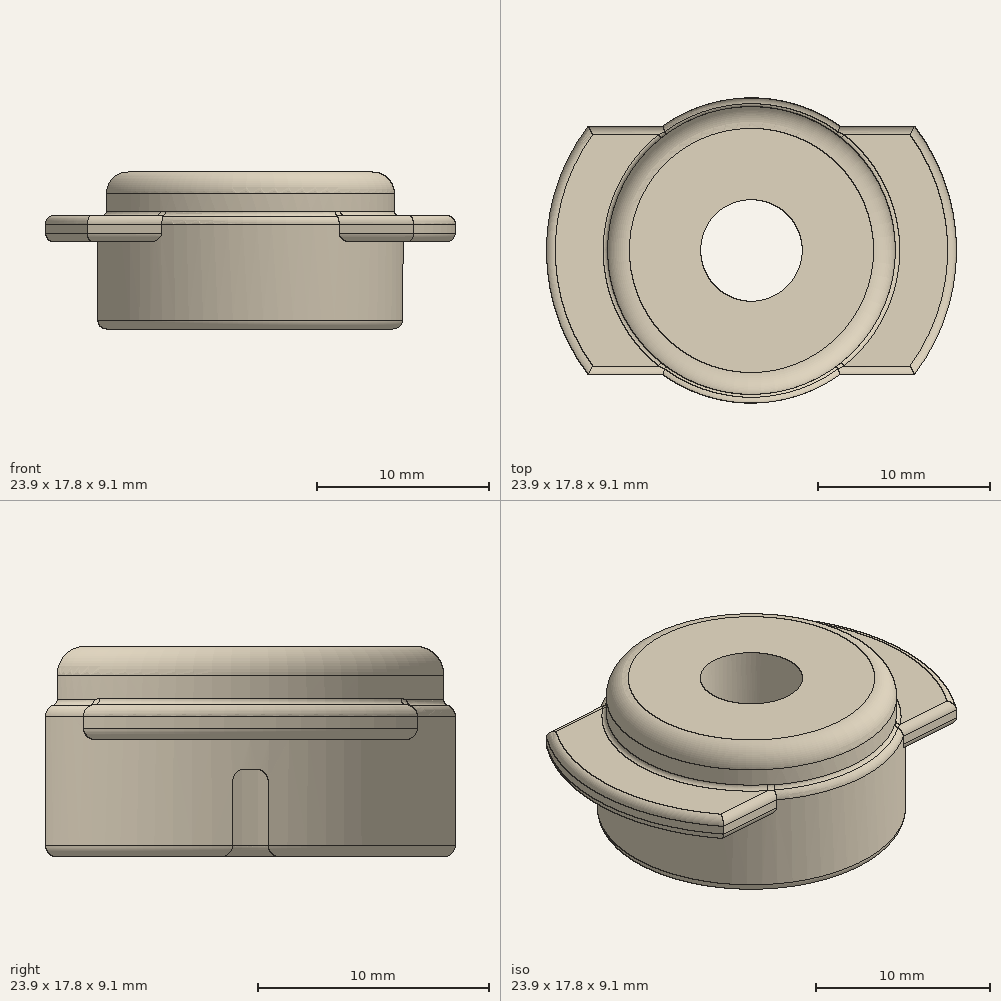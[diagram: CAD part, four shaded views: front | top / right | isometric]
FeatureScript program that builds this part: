
annotation { "Feature Type Name" : "Feature", "Feature Type Description" : "" }
export const myFeature = defineFeature(function(context is Context, id is Id, definition is map)
    precondition{}
    {
        {
            var Q0;
            Q0=qCreatedBy(makeId("Top.planeOp"),FACE);
            var sketch = newSketch(context, id + "F0", { "sketchPlane" : qUnion([Q0])});
            skCircle(sketch, "E0", {"center": v(0, 0) * mm, "radius": 11.94 * mm});
            skSolve(sketch);
        }
        {
            var Q0;
            Q0=makeQuery(id+"F0.imprint","IMPRINT",FACE,{"disambiguationData":[TD([[makeQuery(id+"F0.imprint","IMPRINT",EDGE,{"derivedFrom":sQuery(id+"F0.wireOp",EDGE,"E0")}),1.0]])]});
            var sketch = newSketch(context, id + "F1", { "sketchPlane" : qUnion([Q0])});
            skLineSegment(sketch, "E1", {"start": v(9.5, 7.24) * mm, "end": v(-9.5, 7.24) * mm});
            skLineSegment(sketch, "E2", {"start": v(9.5, -7.24) * mm, "end": v(-9.5, -7.24) * mm});
            skLineSegment(sketch, "E3", {"start": v(-9.5, 7.24) * mm, "end": v(-9.5, -7.24) * mm, "construction": true});
            skLineSegment(sketch, "E4", {"start": v(9.5, 7.24) * mm, "end": v(9.5, -7.24) * mm, "construction": true});
            skSolve(sketch);
        }
        {
            var Q0;
            Q0=qSketchRegion(id+"F0",true);
            extrude(context, id + "F2", {"entities" : qUnion([Q0]), "depth" : 1.52 * mm, "offsetDistance" : 25.4 * mm});
        }
        {
            var Q0;
            {var subQ0=sQuery(id+"F1.wireOp",EDGE,"E1");Q0=makeQuery(id+"F1.imprint","IMPRINT",FACE,{"disambiguationData":[TD([[makeQuery(id+"F1.imprint","IMPRINT",EDGE,{"derivedFrom":subQ0}),-1.0]])]});}
            var Q1;
            {var subQ0=sQuery(id+"F1.wireOp",EDGE,"E2");Q1=makeQuery(id+"F1.imprint","IMPRINT",FACE,{"disambiguationData":[TD([[makeQuery(id+"F1.imprint","IMPRINT",EDGE,{"derivedFrom":subQ0}),1.0]])]});}
            extrude(context, id + "F3", {"entities" : qUnion([Q0, Q1]), "operationType" : NewBodyOperationType.REMOVE, "depth" : 2.54 * mm, "offsetDistance" : 25.4 * mm, "hasSecondDirection" : true, "secondDirectionOppositeDirection" : true, "secondDirectionDepth" : 25.4 * mm});
        }
        {
            var Q0;
            Q0=makeQuery(id+"F2.opExtrude","CAP_FACE",FACE,{"disambiguationData":[OSD([sQuery(id+"F0.wireOp",EDGE,"E0")])],"isStart":true});
            var sketch = newSketch(context, id + "F4", { "sketchPlane" : qUnion([Q0])});
            skCircle(sketch, "E5", {"center": v(0, 0) * mm, "radius": 8.9 * mm});
            skSolve(sketch);
        }
        {
            var Q0;
            Q0=qSketchRegion(id+"F4",true);
            extrude(context, id + "F5", {"entities" : qUnion([Q0]), "operationType" : NewBodyOperationType.ADD, "oppositeDirection" : true, "depth" : 1.52 * mm, "offsetDistance" : 25.4 * mm});
        }
        {
            var Q0;
            Q0=makeQuery(id+"F5.boolean.opBoolean","MERGE",FACE,{"derivedFrom":[makeQuery(id+"F2.opExtrude","CAP_FACE",FACE,{"disambiguationData":[OSD([sQuery(id+"F0.wireOp",EDGE,"E0")])],"isStart":true}),makeQuery(id+"F5.opExtrude","CAP_FACE",FACE,{"disambiguationData":[OSD([sQuery(id+"F4.wireOp",EDGE,"E5")])],"isStart":true})]});
            var sketch = newSketch(context, id + "F6", { "sketchPlane" : qUnion([Q0])});
            skCircle(sketch, "E6", {"center": v(0, 0) * mm, "radius": 8.9 * mm});
            skSolve(sketch);
        }
        {
            var Q0;
            Q0=qSketchRegion(id+"F6",true);
            extrude(context, id + "F7", {"entities" : qUnion([Q0]), "operationType" : NewBodyOperationType.ADD, "depth" : 5.08 * mm, "offsetDistance" : 25.4 * mm});
        }
        {
            var Q0;
            Q0=makeQuery(id+"F7.opExtrude","CAP_FACE",FACE,{"disambiguationData":[OSD([sQuery(id+"F6.wireOp",EDGE,"E6")])],"isStart":false});
            var sketch = newSketch(context, id + "F8", { "sketchPlane" : qUnion([Q0])});
            skCircle(sketch, "E7", {"center": v(0, 0) * mm, "radius": 7.37 * mm});
            skSolve(sketch);
        }
        {
            var Q0;
            Q0=qSketchRegion(id+"F8",true);
            extrude(context, id + "F9", {"entities" : qUnion([Q0]), "operationType" : NewBodyOperationType.REMOVE, "oppositeDirection" : true, "depth" : 5.08 * mm, "offsetDistance" : 25.4 * mm});
        }
        {
            var Q0;
            Q0=makeQuery(id+"F7.opExtrude","CAP_FACE",FACE,{"disambiguationData":[OSD([sQuery(id+"F6.wireOp",EDGE,"E6")])],"isStart":false});
            var sketch = newSketch(context, id + "F10", { "sketchPlane" : qUnion([Q0])});
            skLineSegment(sketch, "E8", {"start": v(8.86, -0.76) * mm, "end": v(7.33, -0.76) * mm});
            skLineSegment(sketch, "E9", {"start": v(8.86, 0.76) * mm, "end": v(7.33, 0.76) * mm});
            skLineSegment(sketch, "E10", {"start": v(0, 0) * mm, "end": v(8.9, 0) * mm, "construction": true});
            skArc(sketch, "E11", {"start": v(8.86, -0.76) * mm, "mid": v(8.9, 0) * mm, "end": v(8.86, 0.76) * mm});
            skArc(sketch, "E12", {"start": v(7.33, -0.76) * mm, "mid": v(7.37, 0) * mm, "end": v(7.33, 0.76) * mm});
            skSolve(sketch);
        }
        {
            var Q0;
            Q0=qCreatedBy(makeId("Front.planeOp"),FACE);
            var sketch = newSketch(context, id + "F11", { "sketchPlane" : qUnion([Q0])});
            skLineSegment(sketch, "E13", {"start": v(0, 0) * mm, "end": v(0, -7.62) * mm, "construction": true});
            skSolve(sketch);
        }
        {
            var Q0;
            Q0=makeQuery(id+"F10.imprint","IMPRINT",FACE,{"disambiguationData":[TD([[makeQuery(id+"F10.imprint","IMPRINT",EDGE,{"derivedFrom":sQuery(id+"F10.wireOp",EDGE,"E8")}),-1.0]])]});
            var Q1;
            Q1=makeQuery(id+"FOOJxRczT3KKHVt_1.3.F10.imprint","IMPRINT",FACE,{"disambiguationData":[TD([[makeQuery(id+"FOOJxRczT3KKHVt_1.3.F10.imprint","IMPRINT",EDGE,{"derivedFrom":sQuery(id+"FOOJxRczT3KKHVt_1.3.F10.wireOp",EDGE,"E8")}),-1.0]])]});
            var Q2;
            Q2=makeQuery(id+"FOOJxRczT3KKHVt_1.2.F10.imprint","IMPRINT",FACE,{"disambiguationData":[TD([[makeQuery(id+"FOOJxRczT3KKHVt_1.2.F10.imprint","IMPRINT",EDGE,{"derivedFrom":sQuery(id+"FOOJxRczT3KKHVt_1.2.F10.wireOp",EDGE,"E8")}),-1.0]])]});
            var Q3;
            Q3=makeQuery(id+"FOOJxRczT3KKHVt_1.1.F10.imprint","IMPRINT",FACE,{"disambiguationData":[TD([[makeQuery(id+"FOOJxRczT3KKHVt_1.1.F10.imprint","IMPRINT",EDGE,{"derivedFrom":sQuery(id+"FOOJxRczT3KKHVt_1.1.F10.wireOp",EDGE,"E8")}),-1.0]])]});
            extrude(context, id + "F12", {"entities" : qUnion([Q0, Q1, Q2, Q3]), "operationType" : NewBodyOperationType.REMOVE, "oppositeDirection" : true, "depth" : 3.8 * mm, "offsetDistance" : 25.4 * mm});
        }
        {
            var Q0;
            Q0=makeQuery(id+"F12.boolean.opBoolean","COPY",EDGE,{"derivedFrom":makeQuery(id+"F12.opExtrude","CAP_EDGE",EDGE,{"disambiguationData":[OSD([sQuery(id+"FOOJxRczT3KKHVt_1.2.F10.wireOp",EDGE,"E9")])],"isStart":false})});
            var Q1;
            Q1=makeQuery(id+"F12.boolean.opBoolean","COPY",EDGE,{"derivedFrom":makeQuery(id+"F12.opExtrude","CAP_EDGE",EDGE,{"disambiguationData":[OSD([sQuery(id+"FOOJxRczT3KKHVt_1.2.F10.wireOp",EDGE,"E8")])],"isStart":false})});
            var Q2;
            Q2=makeQuery(id+"F12.boolean.opBoolean","COPY",EDGE,{"derivedFrom":makeQuery(id+"F12.opExtrude","CAP_EDGE",EDGE,{"disambiguationData":[OSD([sQuery(id+"FOOJxRczT3KKHVt_1.1.F10.wireOp",EDGE,"E9")])],"isStart":false})});
            var Q3;
            Q3=makeQuery(id+"F12.boolean.opBoolean","COPY",EDGE,{"derivedFrom":makeQuery(id+"F12.opExtrude","CAP_EDGE",EDGE,{"disambiguationData":[OSD([sQuery(id+"FOOJxRczT3KKHVt_1.3.F10.wireOp",EDGE,"E8")])],"isStart":false})});
            var Q4;
            Q4=makeQuery(id+"F12.boolean.opBoolean","COPY",EDGE,{"derivedFrom":makeQuery(id+"F12.opExtrude","CAP_EDGE",EDGE,{"disambiguationData":[OSD([sQuery(id+"F10.wireOp",EDGE,"E9")])],"isStart":false})});
            var Q5;
            Q5=makeQuery(id+"F12.boolean.opBoolean","COPY",EDGE,{"derivedFrom":makeQuery(id+"F12.opExtrude","CAP_EDGE",EDGE,{"disambiguationData":[OSD([sQuery(id+"FOOJxRczT3KKHVt_1.3.F10.wireOp",EDGE,"E9")])],"isStart":false})});
            var Q6;
            Q6=makeQuery(id+"F12.boolean.opBoolean","COPY",EDGE,{"derivedFrom":makeQuery(id+"F12.opExtrude","CAP_EDGE",EDGE,{"disambiguationData":[OSD([sQuery(id+"F10.wireOp",EDGE,"E8")])],"isStart":false})});
            var Q7;
            Q7=makeQuery(id+"F12.boolean.opBoolean","COPY",EDGE,{"derivedFrom":makeQuery(id+"F12.opExtrude","CAP_EDGE",EDGE,{"disambiguationData":[OSD([sQuery(id+"FOOJxRczT3KKHVt_1.1.F10.wireOp",EDGE,"E8")])],"isStart":false})});
            fillet(context, id + "F13", {"entities" : qUnion([Q0, Q1, Q2, Q3, Q4, Q5, Q6, Q7]), "radius" : 0.5 * mm, "tangentPropagation" : true, "allowEdgeOverflow" : false});
        }
        {
            var Q0;
            Q0=makeQuery(id+"F12.boolean.opBoolean","COPY",EDGE,{"derivedFrom":makeQuery(id+"F12.opExtrude","SWEPT_EDGE",EDGE,{"disambiguationData":[OSD([sQuery(id+"F6.wireOp",EDGE,"E6"),sQuery(id+"F10.wireOp",EDGE,"E8"),sQuery(id+"F10.wireOp",EDGE,"E11")])]})});
            var Q1;
            Q1=makeQuery(id+"F12.boolean.opBoolean","COPY",EDGE,{"derivedFrom":makeQuery(id+"F12.opExtrude","SWEPT_EDGE",EDGE,{"disambiguationData":[OSD([sQuery(id+"F6.wireOp",EDGE,"E6"),sQuery(id+"F10.wireOp",EDGE,"E9"),sQuery(id+"F10.wireOp",EDGE,"E11")])]})});
            var Q2;
            Q2=makeQuery(id+"F12.boolean.opBoolean","COPY",EDGE,{"derivedFrom":makeQuery(id+"F12.opExtrude","SWEPT_EDGE",EDGE,{"disambiguationData":[OSD([sQuery(id+"F8.wireOp",EDGE,"E7"),sQuery(id+"F10.wireOp",EDGE,"E8"),sQuery(id+"F10.wireOp",EDGE,"E12")])]})});
            var Q3;
            Q3=makeQuery(id+"F12.boolean.opBoolean","COPY",EDGE,{"derivedFrom":makeQuery(id+"F12.opExtrude","SWEPT_EDGE",EDGE,{"disambiguationData":[OSD([sQuery(id+"F8.wireOp",EDGE,"E7"),sQuery(id+"F10.wireOp",EDGE,"E9"),sQuery(id+"F10.wireOp",EDGE,"E12")])]})});
            var Q4;
            {var subQ0=sQuery(id+"F6.wireOp",EDGE,"E6");Q4=makeQuery(id+"F12.boolean.opBoolean","SPLIT",EDGE,{"disambiguationData":[TD([makeQuery(id+"F12.opExtrude","SWEPT_FACE",FACE,{"disambiguationData":[OSD([sQuery(id+"F10.wireOp",EDGE,"E8")])]})])],"derivedFrom":makeQuery(id+"F7.opExtrude","CAP_EDGE",EDGE,{"disambiguationData":[OSD([subQ0])],"isStart":false})});}
            var Q5;
            {var subQ0=sQuery(id+"F8.wireOp",EDGE,"E7");Q5=makeQuery(id+"F12.boolean.opBoolean","SPLIT",EDGE,{"disambiguationData":[TD([makeQuery(id+"F12.opExtrude","SWEPT_FACE",FACE,{"disambiguationData":[OSD([sQuery(id+"F10.wireOp",EDGE,"E8")])]})])],"derivedFrom":makeQuery(id+"F9.boolean.opBoolean","COPY",EDGE,{"derivedFrom":makeQuery(id+"F9.opExtrude","CAP_EDGE",EDGE,{"disambiguationData":[OSD([subQ0])],"isStart":true})})});}
            var Q6;
            {var subQ0=sQuery(id+"F6.wireOp",EDGE,"E6");Q6=makeQuery(id+"F12.boolean.opBoolean","SPLIT",EDGE,{"disambiguationData":[TD([makeQuery(id+"F12.opExtrude","SWEPT_FACE",FACE,{"disambiguationData":[OSD([sQuery(id+"F10.wireOp",EDGE,"E9")])]})])],"derivedFrom":makeQuery(id+"F7.opExtrude","CAP_EDGE",EDGE,{"disambiguationData":[OSD([subQ0])],"isStart":false})});}
            var Q7;
            {var subQ0=sQuery(id+"F8.wireOp",EDGE,"E7");Q7=makeQuery(id+"F12.boolean.opBoolean","SPLIT",EDGE,{"disambiguationData":[TD([makeQuery(id+"F12.opExtrude","SWEPT_FACE",FACE,{"disambiguationData":[OSD([sQuery(id+"F10.wireOp",EDGE,"E9")])]})])],"derivedFrom":makeQuery(id+"F9.boolean.opBoolean","COPY",EDGE,{"derivedFrom":makeQuery(id+"F9.opExtrude","CAP_EDGE",EDGE,{"disambiguationData":[OSD([subQ0])],"isStart":true})})});}
            var Q8;
            Q8=makeQuery(id+"F12.boolean.opBoolean","COPY",EDGE,{"derivedFrom":makeQuery(id+"F12.opExtrude","CAP_EDGE",EDGE,{"disambiguationData":[OSD([sQuery(id+"F10.wireOp",EDGE,"E9")])],"isStart":true})});
            var Q9;
            Q9=makeQuery(id+"F12.boolean.opBoolean","COPY",EDGE,{"derivedFrom":makeQuery(id+"F12.opExtrude","CAP_EDGE",EDGE,{"disambiguationData":[OSD([sQuery(id+"F10.wireOp",EDGE,"E8")])],"isStart":true})});
            var Q10;
            {var subQ0=sQuery(id+"F6.wireOp",EDGE,"E6");Q10=makeQuery(id+"F12.boolean.opBoolean","SPLIT",EDGE,{"disambiguationData":[TD([makeQuery(id+"F12.opExtrude","SWEPT_FACE",FACE,{"disambiguationData":[OSD([sQuery(id+"FOOJxRczT3KKHVt_1.2.F10.wireOp",EDGE,"E9")])]})])],"derivedFrom":makeQuery(id+"F7.opExtrude","CAP_EDGE",EDGE,{"disambiguationData":[OSD([subQ0])],"isStart":false})});}
            var Q11;
            {var subQ0=sQuery(id+"F8.wireOp",EDGE,"E7");Q11=makeQuery(id+"F12.boolean.opBoolean","SPLIT",EDGE,{"disambiguationData":[TD([makeQuery(id+"F12.opExtrude","SWEPT_FACE",FACE,{"disambiguationData":[OSD([sQuery(id+"FOOJxRczT3KKHVt_1.2.F10.wireOp",EDGE,"E9")])]})])],"derivedFrom":makeQuery(id+"F9.boolean.opBoolean","COPY",EDGE,{"derivedFrom":makeQuery(id+"F9.opExtrude","CAP_EDGE",EDGE,{"disambiguationData":[OSD([subQ0])],"isStart":true})})});}
            var Q12;
            Q12=makeQuery(id+"F12.boolean.opBoolean","COPY",EDGE,{"derivedFrom":makeQuery(id+"F12.opExtrude","CAP_EDGE",EDGE,{"disambiguationData":[OSD([sQuery(id+"FOOJxRczT3KKHVt_1.3.F10.wireOp",EDGE,"E8")])],"isStart":true})});
            var Q13;
            Q13=makeQuery(id+"F12.boolean.opBoolean","COPY",EDGE,{"derivedFrom":makeQuery(id+"F12.opExtrude","CAP_EDGE",EDGE,{"disambiguationData":[OSD([sQuery(id+"FOOJxRczT3KKHVt_1.3.F10.wireOp",EDGE,"E9")])],"isStart":true})});
            var Q14;
            Q14=makeQuery(id+"F12.boolean.opBoolean","COPY",EDGE,{"derivedFrom":makeQuery(id+"F12.opExtrude","SWEPT_EDGE",EDGE,{"disambiguationData":[OSD([sQuery(id+"FOOJxRczT3KKHVt_1.3.F10.wireOp",EDGE,"E8"),sQuery(id+"FOOJxRczT3KKHVt_1.3.F10.wireOp",EDGE,"E11")])]})});
            var Q15;
            Q15=makeQuery(id+"F12.boolean.opBoolean","COPY",EDGE,{"derivedFrom":makeQuery(id+"F12.opExtrude","SWEPT_EDGE",EDGE,{"disambiguationData":[OSD([sQuery(id+"FOOJxRczT3KKHVt_1.3.F10.wireOp",EDGE,"E9"),sQuery(id+"FOOJxRczT3KKHVt_1.3.F10.wireOp",EDGE,"E11")])]})});
            var Q16;
            Q16=makeQuery(id+"F12.boolean.opBoolean","COPY",EDGE,{"derivedFrom":makeQuery(id+"F12.opExtrude","CAP_EDGE",EDGE,{"disambiguationData":[OSD([sQuery(id+"FOOJxRczT3KKHVt_1.1.F10.wireOp",EDGE,"E9")])],"isStart":true})});
            var Q17;
            Q17=makeQuery(id+"F12.boolean.opBoolean","COPY",EDGE,{"derivedFrom":makeQuery(id+"F12.opExtrude","CAP_EDGE",EDGE,{"disambiguationData":[OSD([sQuery(id+"FOOJxRczT3KKHVt_1.1.F10.wireOp",EDGE,"E8")])],"isStart":true})});
            var Q18;
            Q18=makeQuery(id+"F12.boolean.opBoolean","COPY",EDGE,{"derivedFrom":makeQuery(id+"F12.opExtrude","SWEPT_EDGE",EDGE,{"disambiguationData":[OSD([sQuery(id+"FOOJxRczT3KKHVt_1.1.F10.wireOp",EDGE,"E9"),sQuery(id+"FOOJxRczT3KKHVt_1.1.F10.wireOp",EDGE,"E11")])]})});
            var Q19;
            Q19=makeQuery(id+"F12.boolean.opBoolean","COPY",EDGE,{"derivedFrom":makeQuery(id+"F12.opExtrude","CAP_EDGE",EDGE,{"disambiguationData":[OSD([sQuery(id+"FOOJxRczT3KKHVt_1.2.F10.wireOp",EDGE,"E9")])],"isStart":true})});
            var Q20;
            Q20=makeQuery(id+"F12.boolean.opBoolean","COPY",EDGE,{"derivedFrom":makeQuery(id+"F12.opExtrude","CAP_EDGE",EDGE,{"disambiguationData":[OSD([sQuery(id+"FOOJxRczT3KKHVt_1.2.F10.wireOp",EDGE,"E8")])],"isStart":true})});
            var Q21;
            {var subQ0=sQuery(id+"F8.wireOp",EDGE,"E7");Q21=makeQuery(id+"F12.boolean.opBoolean","SPLIT",EDGE,{"disambiguationData":[TD([makeQuery(id+"F12.opExtrude","SWEPT_FACE",FACE,{"disambiguationData":[OSD([sQuery(id+"FOOJxRczT3KKHVt_1.1.F10.wireOp",EDGE,"E9")])]})])],"derivedFrom":makeQuery(id+"F9.boolean.opBoolean","COPY",EDGE,{"derivedFrom":makeQuery(id+"F9.opExtrude","CAP_EDGE",EDGE,{"disambiguationData":[OSD([subQ0])],"isStart":true})})});}
            var Q22;
            {var subQ0=sQuery(id+"F6.wireOp",EDGE,"E6");Q22=makeQuery(id+"F12.boolean.opBoolean","SPLIT",EDGE,{"disambiguationData":[TD([makeQuery(id+"F12.opExtrude","SWEPT_FACE",FACE,{"disambiguationData":[OSD([sQuery(id+"FOOJxRczT3KKHVt_1.1.F10.wireOp",EDGE,"E9")])]})])],"derivedFrom":makeQuery(id+"F7.opExtrude","CAP_EDGE",EDGE,{"disambiguationData":[OSD([subQ0])],"isStart":false})});}
            var Q23;
            {var subQ0=sQuery(id+"F6.wireOp",EDGE,"E6");Q23=makeQuery(id+"F12.boolean.opBoolean","SPLIT",FACE,{"disambiguationData":[TD([makeQuery(id+"F12.opExtrude","SWEPT_FACE",FACE,{"disambiguationData":[OSD([sQuery(id+"FOOJxRczT3KKHVt_1.1.F10.wireOp",EDGE,"E9")])]})])],"derivedFrom":makeQuery(id+"F7.opExtrude","CAP_FACE",FACE,{"disambiguationData":[OSD([subQ0])],"isStart":false})});}
            var Q24;
            Q24=makeQuery(id+"F12.boolean.opBoolean","COPY",EDGE,{"derivedFrom":makeQuery(id+"F12.opExtrude","SWEPT_EDGE",EDGE,{"disambiguationData":[OSD([sQuery(id+"FOOJxRczT3KKHVt_1.2.F10.wireOp",EDGE,"E8"),sQuery(id+"FOOJxRczT3KKHVt_1.2.F10.wireOp",EDGE,"E11")])]})});
            var Q25;
            Q25=makeQuery(id+"F12.boolean.opBoolean","COPY",EDGE,{"derivedFrom":makeQuery(id+"F12.opExtrude","SWEPT_EDGE",EDGE,{"disambiguationData":[OSD([sQuery(id+"FOOJxRczT3KKHVt_1.2.F10.wireOp",EDGE,"E9"),sQuery(id+"FOOJxRczT3KKHVt_1.2.F10.wireOp",EDGE,"E11")])]})});
            var Q26;
            Q26=makeQuery(id+"F12.boolean.opBoolean","COPY",EDGE,{"derivedFrom":makeQuery(id+"F12.opExtrude","SWEPT_EDGE",EDGE,{"disambiguationData":[OSD([sQuery(id+"FOOJxRczT3KKHVt_1.2.F10.wireOp",EDGE,"E9"),sQuery(id+"FOOJxRczT3KKHVt_1.2.F10.wireOp",EDGE,"E12")])]})});
            var Q27;
            Q27=makeQuery(id+"F12.boolean.opBoolean","COPY",EDGE,{"derivedFrom":makeQuery(id+"F12.opExtrude","SWEPT_EDGE",EDGE,{"disambiguationData":[OSD([sQuery(id+"FOOJxRczT3KKHVt_1.2.F10.wireOp",EDGE,"E8"),sQuery(id+"FOOJxRczT3KKHVt_1.2.F10.wireOp",EDGE,"E12")])]})});
            var Q28;
            Q28=makeQuery(id+"F12.boolean.opBoolean","COPY",EDGE,{"derivedFrom":makeQuery(id+"F12.opExtrude","SWEPT_EDGE",EDGE,{"disambiguationData":[OSD([sQuery(id+"FOOJxRczT3KKHVt_1.1.F10.wireOp",EDGE,"E9"),sQuery(id+"FOOJxRczT3KKHVt_1.1.F10.wireOp",EDGE,"E12")])]})});
            var Q29;
            Q29=makeQuery(id+"F12.boolean.opBoolean","COPY",EDGE,{"derivedFrom":makeQuery(id+"F12.opExtrude","SWEPT_EDGE",EDGE,{"disambiguationData":[OSD([sQuery(id+"FOOJxRczT3KKHVt_1.1.F10.wireOp",EDGE,"E8"),sQuery(id+"FOOJxRczT3KKHVt_1.1.F10.wireOp",EDGE,"E12")])]})});
            var Q30;
            Q30=makeQuery(id+"F12.boolean.opBoolean","COPY",EDGE,{"derivedFrom":makeQuery(id+"F12.opExtrude","SWEPT_EDGE",EDGE,{"disambiguationData":[OSD([sQuery(id+"FOOJxRczT3KKHVt_1.3.F10.wireOp",EDGE,"E8"),sQuery(id+"FOOJxRczT3KKHVt_1.3.F10.wireOp",EDGE,"E12")])]})});
            var Q31;
            Q31=makeQuery(id+"F12.boolean.opBoolean","COPY",EDGE,{"derivedFrom":makeQuery(id+"F12.opExtrude","SWEPT_EDGE",EDGE,{"disambiguationData":[OSD([sQuery(id+"FOOJxRczT3KKHVt_1.3.F10.wireOp",EDGE,"E9"),sQuery(id+"FOOJxRczT3KKHVt_1.3.F10.wireOp",EDGE,"E12")])]})});
            fillet(context, id + "F14", {"entities" : qUnion([Q0, Q1, Q2, Q3, Q4, Q5, Q6, Q7, Q8, Q9, Q10, Q11, Q12, Q13, Q14, Q15, Q16, Q17, Q18, Q19, Q20, Q21, Q22, Q23, Q24, Q25, Q26, Q27, Q28, Q29, Q30, Q31]), "radius" : 0.5 * mm, "tangentPropagation" : true, "allowEdgeOverflow" : false});
        }
        {
            var Q0;
            {var subQ0=sQuery(id+"F4.wireOp",EDGE,"E5");Q0=makeQuery(id+"F5.boolean.opBoolean","SPLIT",EDGE,{"disambiguationData":[TD([makeQuery(id+"F3.boolean.opBoolean","COPY",FACE,{"derivedFrom":makeQuery(id+"F3.opExtrude","SWEPT_FACE",FACE,{"disambiguationData":[OSD([sQuery(id+"F1.wireOp",EDGE,"E1")])]})})])],"derivedFrom":makeQuery(id+"F5.opExtrude","CAP_EDGE",EDGE,{"disambiguationData":[OSD([subQ0])],"isStart":false})});}
            var Q1;
            {var subQ0=sQuery(id+"F4.wireOp",EDGE,"E5");Q1=makeQuery(id+"F5.boolean.opBoolean","SPLIT",EDGE,{"disambiguationData":[TD([makeQuery(id+"F3.boolean.opBoolean","COPY",FACE,{"derivedFrom":makeQuery(id+"F3.opExtrude","SWEPT_FACE",FACE,{"disambiguationData":[OSD([sQuery(id+"F1.wireOp",EDGE,"E2")])]})})])],"derivedFrom":makeQuery(id+"F5.opExtrude","CAP_EDGE",EDGE,{"disambiguationData":[OSD([subQ0])],"isStart":false})});}
            var Q2;
            Q2=makeQuery(id+"F5.boolean.opBoolean","SPLIT",EDGE,{"disambiguationData":[OD(0.0)],"derivedFrom":makeQuery(id+"F3.boolean.opBoolean","INTERSECT",EDGE,{"derivedFrom":[makeQuery(id+"F2.opExtrude","CAP_FACE",FACE,{"disambiguationData":[OSD([sQuery(id+"F0.wireOp",EDGE,"E0")])],"isStart":false}),makeQuery(id+"F3.opExtrude","SWEPT_FACE",FACE,{"disambiguationData":[OSD([sQuery(id+"F1.wireOp",EDGE,"E2")])]})]})});
            var Q3;
            Q3=makeQuery(id+"F5.boolean.opBoolean","SPLIT",EDGE,{"disambiguationData":[OD(0.0)],"derivedFrom":makeQuery(id+"F3.boolean.opBoolean","INTERSECT",EDGE,{"derivedFrom":[makeQuery(id+"F2.opExtrude","CAP_FACE",FACE,{"disambiguationData":[OSD([sQuery(id+"F0.wireOp",EDGE,"E0")])],"isStart":false}),makeQuery(id+"F3.opExtrude","SWEPT_FACE",FACE,{"disambiguationData":[OSD([sQuery(id+"F1.wireOp",EDGE,"E1")])]})]})});
            var Q4;
            Q4=makeQuery(id+"F3.boolean.opBoolean","SPLIT",EDGE,{"disambiguationData":[OD(0.0)],"derivedFrom":makeQuery(id+"F2.opExtrude","CAP_EDGE",EDGE,{"disambiguationData":[OSD([sQuery(id+"F0.wireOp",EDGE,"E0")])],"isStart":false})});
            var Q5;
            Q5=makeQuery(id+"F5.boolean.opBoolean","SPLIT",EDGE,{"disambiguationData":[OD(1.0)],"derivedFrom":makeQuery(id+"F3.boolean.opBoolean","INTERSECT",EDGE,{"derivedFrom":[makeQuery(id+"F2.opExtrude","CAP_FACE",FACE,{"disambiguationData":[OSD([sQuery(id+"F0.wireOp",EDGE,"E0")])],"isStart":false}),makeQuery(id+"F3.opExtrude","SWEPT_FACE",FACE,{"disambiguationData":[OSD([sQuery(id+"F1.wireOp",EDGE,"E1")])]})]})});
            var Q6;
            Q6=makeQuery(id+"F3.boolean.opBoolean","SPLIT",EDGE,{"disambiguationData":[OD(1.0)],"derivedFrom":makeQuery(id+"F2.opExtrude","CAP_EDGE",EDGE,{"disambiguationData":[OSD([sQuery(id+"F0.wireOp",EDGE,"E0")])],"isStart":false})});
            var Q7;
            Q7=makeQuery(id+"F5.boolean.opBoolean","SPLIT",EDGE,{"disambiguationData":[OD(1.0)],"derivedFrom":makeQuery(id+"F3.boolean.opBoolean","INTERSECT",EDGE,{"derivedFrom":[makeQuery(id+"F2.opExtrude","CAP_FACE",FACE,{"disambiguationData":[OSD([sQuery(id+"F0.wireOp",EDGE,"E0")])],"isStart":false}),makeQuery(id+"F3.opExtrude","SWEPT_FACE",FACE,{"disambiguationData":[OSD([sQuery(id+"F1.wireOp",EDGE,"E2")])]})]})});
            var Q8;
            Q8=makeQuery(id+"F3.boolean.opBoolean","SPLIT",EDGE,{"disambiguationData":[OD(0.0)],"derivedFrom":makeQuery(id+"F2.opExtrude","CAP_EDGE",EDGE,{"disambiguationData":[OSD([sQuery(id+"F0.wireOp",EDGE,"E0")])],"isStart":true})});
            var Q9;
            Q9=makeQuery(id+"F3.boolean.opBoolean","SPLIT",EDGE,{"disambiguationData":[OD(1.0)],"derivedFrom":makeQuery(id+"F2.opExtrude","CAP_EDGE",EDGE,{"disambiguationData":[OSD([sQuery(id+"F0.wireOp",EDGE,"E0")])],"isStart":true})});
            var Q10;
            Q10=makeQuery(id+"F5.boolean.opBoolean","SPLIT",EDGE,{"disambiguationData":[OD(1.0)],"derivedFrom":makeQuery(id+"F3.boolean.opBoolean","INTERSECT",EDGE,{"derivedFrom":[makeQuery(id+"F2.opExtrude","CAP_FACE",FACE,{"disambiguationData":[OSD([sQuery(id+"F0.wireOp",EDGE,"E0")])],"isStart":true}),makeQuery(id+"F3.opExtrude","SWEPT_FACE",FACE,{"disambiguationData":[OSD([sQuery(id+"F1.wireOp",EDGE,"E2")])]})]})});
            var Q11;
            Q11=makeQuery(id+"F5.boolean.opBoolean","SPLIT",EDGE,{"disambiguationData":[OD(1.0)],"derivedFrom":makeQuery(id+"F3.boolean.opBoolean","INTERSECT",EDGE,{"derivedFrom":[makeQuery(id+"F2.opExtrude","CAP_FACE",FACE,{"disambiguationData":[OSD([sQuery(id+"F0.wireOp",EDGE,"E0")])],"isStart":true}),makeQuery(id+"F3.opExtrude","SWEPT_FACE",FACE,{"disambiguationData":[OSD([sQuery(id+"F1.wireOp",EDGE,"E1")])]})]})});
            var Q12;
            Q12=makeQuery(id+"F5.boolean.opBoolean","SPLIT",EDGE,{"disambiguationData":[OD(0.0)],"derivedFrom":makeQuery(id+"F3.boolean.opBoolean","INTERSECT",EDGE,{"derivedFrom":[makeQuery(id+"F2.opExtrude","CAP_FACE",FACE,{"disambiguationData":[OSD([sQuery(id+"F0.wireOp",EDGE,"E0")])],"isStart":true}),makeQuery(id+"F3.opExtrude","SWEPT_FACE",FACE,{"disambiguationData":[OSD([sQuery(id+"F1.wireOp",EDGE,"E1")])]})]})});
            var Q13;
            Q13=makeQuery(id+"F5.boolean.opBoolean","SPLIT",EDGE,{"disambiguationData":[OD(0.0)],"derivedFrom":makeQuery(id+"F3.boolean.opBoolean","INTERSECT",EDGE,{"derivedFrom":[makeQuery(id+"F2.opExtrude","CAP_FACE",FACE,{"disambiguationData":[OSD([sQuery(id+"F0.wireOp",EDGE,"E0")])],"isStart":true}),makeQuery(id+"F3.opExtrude","SWEPT_FACE",FACE,{"disambiguationData":[OSD([sQuery(id+"F1.wireOp",EDGE,"E2")])]})]})});
            fillet(context, id + "F15", {"entities" : qUnion([Q0, Q1, Q2, Q3, Q4, Q5, Q6, Q7, Q8, Q9, Q10, Q11, Q12, Q13]), "radius" : 0.5 * mm, "tangentPropagation" : true, "allowEdgeOverflow" : false});
        }
        {
            var Q0;
            Q0=makeQuery(id+"F9.boolean.opBoolean","COPY",FACE,{"derivedFrom":makeQuery(id+"F9.opExtrude","CAP_FACE",FACE,{"disambiguationData":[OSD([sQuery(id+"F8.wireOp",EDGE,"E7")])],"isStart":false})});
            var sketch = newSketch(context, id + "F16", { "sketchPlane" : qUnion([Q0])});
            skCircle(sketch, "E14", {"center": v(0, 0) * mm, "radius": 7.37 * mm});
            skSolve(sketch);
        }
        {
            var Q0;
            Q0=qSketchRegion(id+"F16",true);
            extrude(context, id + "F17", {"entities" : qUnion([Q0]), "operationType" : NewBodyOperationType.ADD, "depth" : 1.27 * mm, "offsetDistance" : 25.4 * mm});
        }
        {
            var Q0;
            Q0=makeQuery(id+"F17.opExtrude","CAP_FACE",FACE,{"disambiguationData":[OSD([sQuery(id+"F16.wireOp",EDGE,"E14")])],"isStart":false});
            var sketch = newSketch(context, id + "F18", { "sketchPlane" : qUnion([Q0])});
            skCircle(sketch, "E15", {"center": v(0, 0) * mm, "radius": 2.96 * mm});
            skSolve(sketch);
        }
        {
            var Q0;
            Q0=qSketchRegion(id+"F18",true);
            extrude(context, id + "F19", {"entities" : qUnion([Q0]), "operationType" : NewBodyOperationType.REMOVE, "oppositeDirection" : true, "depth" : 25.4 * mm, "offsetDistance" : 25.4 * mm, "hasSecondDirection" : true, "secondDirectionOppositeDirection" : false, "secondDirectionDepth" : 25.4 * mm});
        }
        {
            var Q0;
            Q0=makeQuery(id+"F5.boolean.opBoolean","MERGE",FACE,{"derivedFrom":[makeQuery(id+"F2.opExtrude","CAP_FACE",FACE,{"disambiguationData":[OSD([sQuery(id+"F0.wireOp",EDGE,"E0")])],"isStart":false}),makeQuery(id+"F5.opExtrude","CAP_FACE",FACE,{"disambiguationData":[OSD([sQuery(id+"F4.wireOp",EDGE,"E5")])],"isStart":false})]});
            var sketch = newSketch(context, id + "F20", { "sketchPlane" : qUnion([Q0])});
            skCircle(sketch, "E16", {"center": v(0, 0) * mm, "radius": 8.38 * mm});
            skSolve(sketch);
        }
        {
            var Q0;
            Q0 = qSketchRegion(id + "F20", true);
            extrude(context, id + "F21", {"entities" : qUnion([Q0]), "operationType" : NewBodyOperationType.ADD, "depth" : 2.54 * mm, "offsetDistance" : 25.4 * mm});
        }
        {
            var Q0;
            Q0=makeQuery(id+"F21.opExtrude","CAP_FACE",FACE,{"disambiguationData":[OSD([sQuery(id+"F20.wireOp",EDGE,"E16")])],"isStart":false});
            var sketch = newSketch(context, id + "F22", { "sketchPlane" : qUnion([Q0])});
            skCircle(sketch, "E17", {"center": v(0, 0) * mm, "radius": 2.96 * mm});
            skSolve(sketch);
        }
        {
            var Q0;
            Q0 = qSketchRegion(id + "F22", true);
            extrude(context, id + "F23", {"entities" : qUnion([Q0]), "operationType" : NewBodyOperationType.REMOVE, "oppositeDirection" : true, "depth" : 25.4 * mm, "offsetDistance" : 25.4 * mm});
        }
        {
            var Q0;
            Q0=makeQuery(id+"F21.opExtrude","CAP_EDGE",EDGE,{"disambiguationData":[OSD([sQuery(id+"F20.wireOp",EDGE,"E16")])],"isStart":false});
            fillet(context, id + "F24", {"entities" : qUnion([Q0]), "radius" : 1.27 * mm, "tangentPropagation" : true, "allowEdgeOverflow" : false});
        }
        {
            var Q0;
            {var subQ2=sQuery(id+"F0.wireOp",EDGE,"E0");var subQ3=makeQuery(id+"F2.opExtrude","CAP_FACE",FACE,{"disambiguationData":[OSD([subQ2])],"isStart":false});var subQ4=sQuery(id+"F1.wireOp",EDGE,"E1");var subQ5=makeQuery(id+"F3.opExtrude","SWEPT_FACE",FACE,{"disambiguationData":[OSD([subQ4])]});var subQ10=sQuery(id+"F20.wireOp",EDGE,"E16");Q0=makeQuery(id+"F21.boolean.opBoolean","SPLIT",EDGE,{"disambiguationData":[TD([makeQuery(id+"F15.opFillet","BLEND_FACE",FACE,{"disambiguationData":[OSD([subQ2,subQ4]),TDD([makeQuery(id+"F5.boolean.opBoolean","SPLIT",EDGE,{"disambiguationData":[OD(0.0)],"derivedFrom":makeQuery(id+"F3.boolean.opBoolean","INTERSECT",EDGE,{"derivedFrom":[subQ3,subQ5]})})])]})])],"derivedFrom":makeQuery(id+"F21.opExtrude","CAP_EDGE",EDGE,{"disambiguationData":[OSD([subQ10])],"isStart":true})});}
            var Q1;
            {var subQ2=sQuery(id+"F0.wireOp",EDGE,"E0");var subQ3=makeQuery(id+"F2.opExtrude","CAP_FACE",FACE,{"disambiguationData":[OSD([subQ2])],"isStart":false});var subQ4=sQuery(id+"F20.wireOp",EDGE,"E16");var subQ5=sQuery(id+"F1.wireOp",EDGE,"E1");var subQ6=makeQuery(id+"F3.opExtrude","SWEPT_FACE",FACE,{"disambiguationData":[OSD([subQ5])]});Q1=makeQuery(id+"F21.boolean.opBoolean","SPLIT",EDGE,{"disambiguationData":[TD([makeQuery(id+"F15.opFillet","BLEND_FACE",FACE,{"disambiguationData":[OSD([subQ2,subQ5]),TDD([makeQuery(id+"F5.boolean.opBoolean","SPLIT",EDGE,{"disambiguationData":[OD(1.0)],"derivedFrom":makeQuery(id+"F3.boolean.opBoolean","INTERSECT",EDGE,{"derivedFrom":[subQ3,subQ6]})})])]})])],"derivedFrom":makeQuery(id+"F21.opExtrude","CAP_EDGE",EDGE,{"disambiguationData":[OSD([subQ4])],"isStart":true})});}
            fillet(context, id + "F25", {"entities" : qUnion([Q0, Q1]), "radius" : 0.25 * mm, "tangentPropagation" : true, "allowEdgeOverflow" : false});
        }
    });
